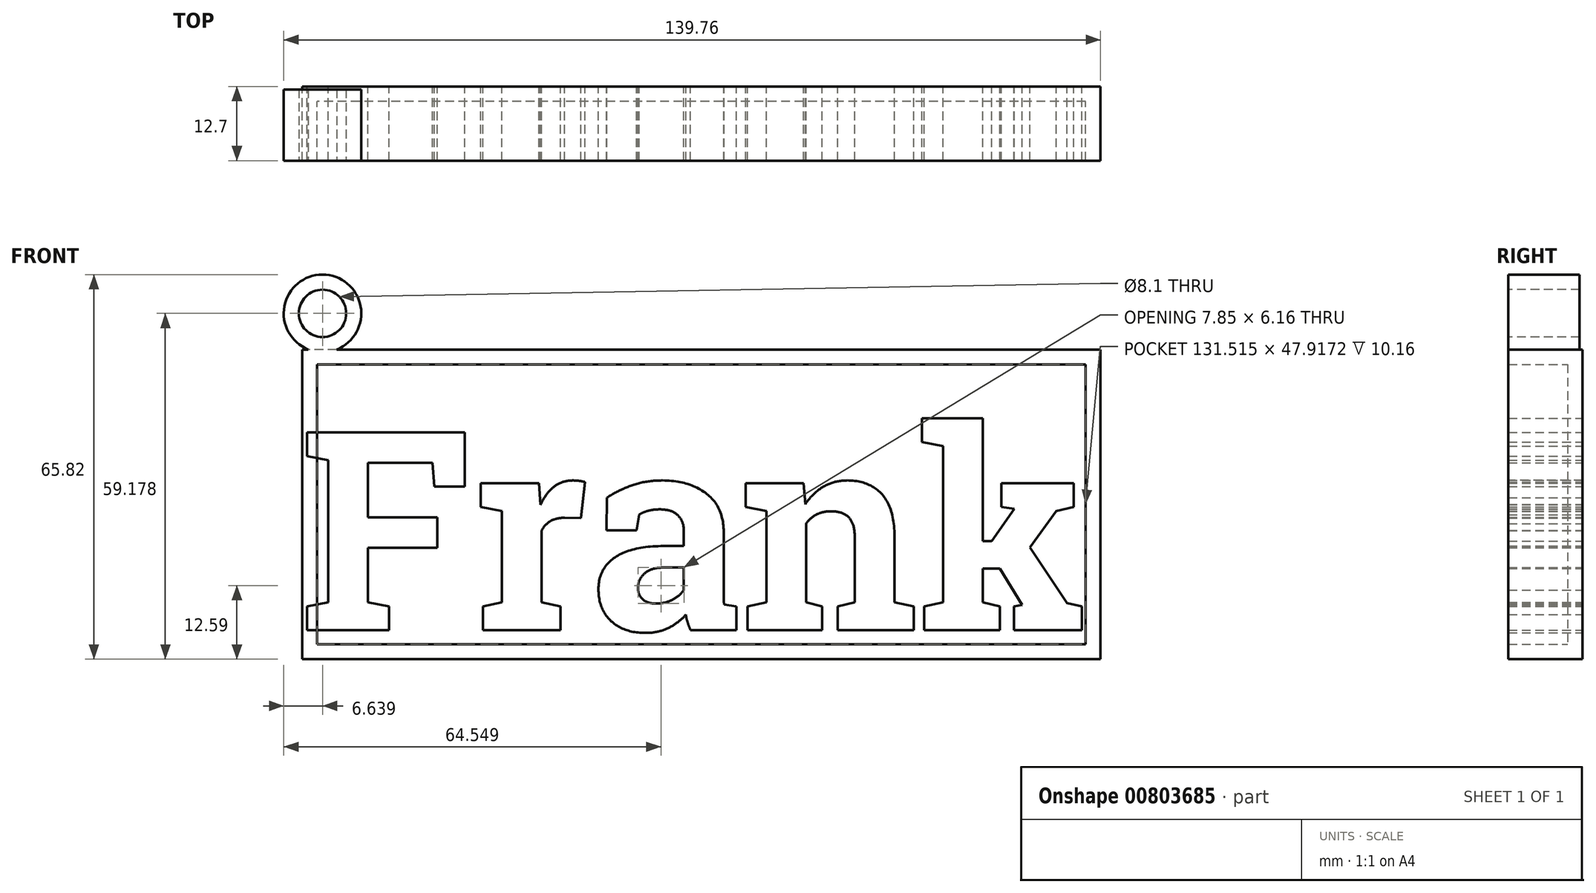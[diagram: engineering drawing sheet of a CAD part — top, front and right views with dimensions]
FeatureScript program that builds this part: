
annotation { "Feature Type Name" : "Feature", "Feature Type Description" : "" }
export const myFeature = defineFeature(function(context is Context, id is Id, definition is map)
    precondition{}
    {
        {
            var Q0;
            Q0=qCreatedBy(makeId("Front.planeOp"),FACE);
            var sketch = newSketch(context, id + "F0", { "sketchPlane" : qUnion([Q0])});
            skText(sketch, "E0", { "text": "Frank", "fontName": "RobotoSlab-Bold.ttf"});
            const initialGuessF0  = {"E0": [-0.06874, -0.02152, 1, 0, 0.03426]};
            skSetInitialGuess(sketch, initialGuessF0);
            skSolve(sketch);
        }
        {
            var Q0;
            Q0 = qSketchRegion(id + "F0", true);
            extrude(context, id + "F1", {"entities" : qUnion([Q0]), "depth" : 12.7 * mm, "offsetDistance" : 25.4 * mm});
        }
        {
            var Q0;
            Q0=qCreatedBy(makeId("Front.planeOp"),FACE);
            var sketch = newSketch(context, id + "F2", { "sketchPlane" : qUnion([Q0])});
            skLineSegment(sketch, "E1.bottom", {"start": v(68.3, 26.5) * mm, "end": v(-68.3, 26.5) * mm});
            skLineSegment(sketch, "E1.top", {"start": v(68.3, -26.5) * mm, "end": v(-68.3, -26.5) * mm});
            skLineSegment(sketch, "E1.left", {"start": v(68.3, 26.5) * mm, "end": v(68.3, -26.5) * mm});
            skLineSegment(sketch, "E1.right", {"start": v(-68.3, 26.5) * mm, "end": v(-68.3, -26.5) * mm});
            skPoint(sketch, "E1.middle", {"position": v(0, 0) * mm});
            skSolve(sketch);
        }
        {
            var Q0;
            Q0=makeQuery(id+"F2.imprint","IMPRINT",FACE,{"disambiguationData":[TD([[makeQuery(id+"F2.imprint","IMPRINT",EDGE,{"derivedFrom":sQuery(id+"F2.wireOp",EDGE,"E1.bottom")}),1.0]])]});
            extrude(context, id + "F3", {"entities" : qUnion([Q0]), "depth" : 12.7 * mm, "offsetDistance" : 25.4 * mm});
        }
        {
            var Q0;
            Q0=makeQuery(id+"F3.opExtrude","CAP_FACE",FACE,{"disambiguationData":[OSD([sQuery(id+"F2.wireOp",EDGE,"E1.bottom"),sQuery(id+"F2.wireOp",EDGE,"E1.top"),sQuery(id+"F2.wireOp",EDGE,"E1.left"),sQuery(id+"F2.wireOp",EDGE,"E1.right")])],"isStart":false});
            shell(context, id + "F4", {"entities" : qUnion([Q0]), "thickness" : 2.54 * mm});
        }
        {
            var Q0;
            Q0=makeQuery(id+"F3.opExtrude","CAP_FACE",FACE,{"disambiguationData":[OSD([sQuery(id+"F2.wireOp",EDGE,"E1.bottom"),sQuery(id+"F2.wireOp",EDGE,"E1.top"),sQuery(id+"F2.wireOp",EDGE,"E1.left"),sQuery(id+"F2.wireOp",EDGE,"E1.right")])],"isStart":false});
            var sketch = newSketch(context, id + "F5", { "sketchPlane" : qUnion([Q0])});
            skCircle(sketch, "E2", {"center": v(-64.82, 32.68) * mm, "radius": 6.64 * mm});
            skCircle(sketch, "E3", {"center": v(-64.82, 32.68) * mm, "radius": 4.05 * mm});
            skSolve(sketch);
        }
        {
            var Q0;
            Q0 = qSketchRegion(id + "F5", true);
            extrude(context, id + "F6", {"entities" : qUnion([Q0]), "operationType" : NewBodyOperationType.ADD, "depth" : 0 * mm, "offsetDistance" : 25.4 * mm, "hasSecondDirection" : true, "secondDirectionOppositeDirection" : true, "secondDirectionDepth" : 12.2 * mm});
        }
    });
